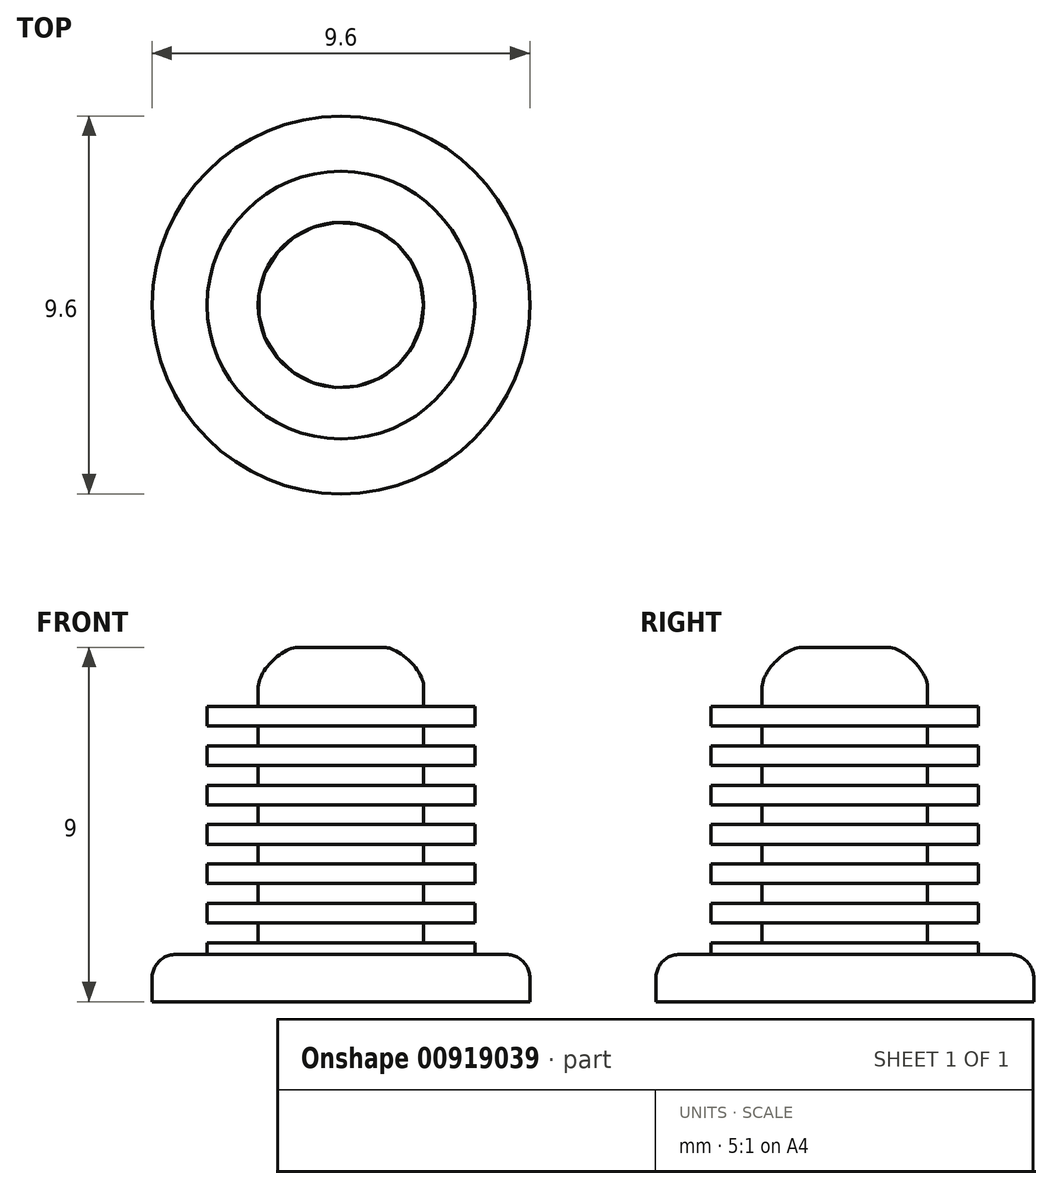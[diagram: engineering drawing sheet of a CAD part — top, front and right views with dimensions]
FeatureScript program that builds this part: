
annotation { "Feature Type Name" : "Feature", "Feature Type Description" : "" }
export const myFeature = defineFeature(function(context is Context, id is Id, definition is map)
    precondition{}
    {
        {
            var Q0;
            Q0=qCreatedBy(makeId("Top.planeOp"),FACE);
            var sketch = newSketch(context, id + "F0", { "sketchPlane" : qUnion([Q0])});
            skCircle(sketch, "E0", {"center": v(0, 0) * mm, "radius": 4.8 * mm});
            skCircle(sketch, "E1", {"center": v(0, 0) * mm, "radius": 2.1 * mm});
            skCircle(sketch, "E2", {"center": v(0, 0) * mm, "radius": 3.4 * mm});
            skSolve(sketch);
        }
        {
            var Q0;
            Q0=makeQuery(id+"F0.imprint","IMPRINT",FACE,{"disambiguationData":[TD([[makeQuery(id+"F0.imprint","IMPRINT",EDGE,{"derivedFrom":sQuery(id+"F0.wireOp",EDGE,"E0")}),1.0]])]});
            var Q1;
            Q1=makeQuery(id+"F0.imprint","IMPRINT",FACE,{"disambiguationData":[TD([[makeQuery(id+"F0.imprint","IMPRINT",EDGE,{"derivedFrom":sQuery(id+"F0.wireOp",EDGE,"E1")}),-1.0]])]});
            extrude(context, id + "F1", {"entities" : qUnion([Q0, Q1]), "depth" : 1.2 * mm, "offsetDistance" : 25 * mm});
        }
        {
            var Q0;
            Q0=makeQuery(id+"F0.imprint","IMPRINT",FACE,{"disambiguationData":[TD([[makeQuery(id+"F0.imprint","IMPRINT",EDGE,{"derivedFrom":sQuery(id+"F0.wireOp",EDGE,"E1")}),1.0]])]});
            var Q1;
            Q1=makeQuery(id+"F0.imprint","IMPRINT",FACE,{"disambiguationData":[TD([[makeQuery(id+"F0.imprint","IMPRINT",EDGE,{"derivedFrom":sQuery(id+"F0.wireOp",EDGE,"E1")}),-1.0]])]});
            extrude(context, id + "F2", {"entities" : qUnion([Q0, Q1]), "operationType" : NewBodyOperationType.ADD, "depth" : 7.5 * mm, "offsetDistance" : 25 * mm});
        }
        {
            var Q0;
            Q0=makeQuery(id+"F0.imprint","IMPRINT",FACE,{"disambiguationData":[TD([[makeQuery(id+"F0.imprint","IMPRINT",EDGE,{"derivedFrom":sQuery(id+"F0.wireOp",EDGE,"E1")}),-1.0]])]});
            extrude(context, id + "F3", {"entities" : qUnion([Q0]), "operationType" : NewBodyOperationType.REMOVE, "depth" : 2 * mm, "offsetDistance" : 25 * mm, "hasSecondDirection" : true, "secondDirectionOppositeDirection" : false, "secondDirectionDepth" : 1.5 * mm});
        }
        {
            var Q0;
            Q0=makeQuery(id+"F0.imprint","IMPRINT",FACE,{"disambiguationData":[TD([[makeQuery(id+"F0.imprint","IMPRINT",EDGE,{"derivedFrom":sQuery(id+"F0.wireOp",EDGE,"E1")}),-1.0]])]});
            extrude(context, id + "F4", {"entities" : qUnion([Q0]), "operationType" : NewBodyOperationType.REMOVE, "depth" : 3 * mm, "offsetDistance" : 25 * mm, "hasSecondDirection" : true, "secondDirectionOppositeDirection" : false, "secondDirectionDepth" : 2.5 * mm});
        }
        {
            var Q0;
            Q0=makeQuery(id+"F0.imprint","IMPRINT",FACE,{"disambiguationData":[TD([[makeQuery(id+"F0.imprint","IMPRINT",EDGE,{"derivedFrom":sQuery(id+"F0.wireOp",EDGE,"E1")}),-1.0]])]});
            var Q1;
            Q1=sQuery(id+"F0.wireOp",EDGE,"E2");
            var Q2;
            Q2=sQuery(id+"F0.wireOp",EDGE,"E1");
            extrude(context, id + "F5", {"entities" : qUnion([Q0]), "operationType" : NewBodyOperationType.REMOVE, "surfaceEntities" : qUnion([Q1, Q2]), "depth" : 4 * mm, "offsetDistance" : 25 * mm, "hasSecondDirection" : true, "secondDirectionOppositeDirection" : false, "secondDirectionDepth" : 3.5 * mm});
        }
        {
            var Q0;
            Q0=makeQuery(id+"F0.imprint","IMPRINT",FACE,{"disambiguationData":[TD([[makeQuery(id+"F0.imprint","IMPRINT",EDGE,{"derivedFrom":sQuery(id+"F0.wireOp",EDGE,"E1")}),-1.0]])]});
            extrude(context, id + "F6", {"entities" : qUnion([Q0]), "operationType" : NewBodyOperationType.REMOVE, "depth" : 5 * mm, "offsetDistance" : 25 * mm, "hasSecondDirection" : true, "secondDirectionOppositeDirection" : false, "secondDirectionDepth" : 4.5 * mm});
        }
        {
            var Q0;
            Q0=makeQuery(id+"F0.imprint","IMPRINT",FACE,{"disambiguationData":[TD([[makeQuery(id+"F0.imprint","IMPRINT",EDGE,{"derivedFrom":sQuery(id+"F0.wireOp",EDGE,"E1")}),-1.0]])]});
            extrude(context, id + "F7", {"entities" : qUnion([Q0]), "operationType" : NewBodyOperationType.REMOVE, "depth" : 6 * mm, "offsetDistance" : 25 * mm, "hasSecondDirection" : true, "secondDirectionOppositeDirection" : false, "secondDirectionDepth" : 5.5 * mm});
        }
        {
            var Q0;
            Q0=makeQuery(id+"F0.imprint","IMPRINT",FACE,{"disambiguationData":[TD([[makeQuery(id+"F0.imprint","IMPRINT",EDGE,{"derivedFrom":sQuery(id+"F0.wireOp",EDGE,"E1")}),1.0]])]});
            extrude(context, id + "F8", {"entities" : qUnion([Q0]), "operationType" : NewBodyOperationType.REMOVE, "depth" : 12 * mm, "offsetDistance" : 25 * mm, "hasSecondDirection" : true, "secondDirectionOppositeDirection" : false, "secondDirectionDepth" : 10 * mm});
        }
        {
            var Q0;
            Q0=makeQuery(id+"F0.imprint","IMPRINT",FACE,{"disambiguationData":[TD([[makeQuery(id+"F0.imprint","IMPRINT",EDGE,{"derivedFrom":sQuery(id+"F0.wireOp",EDGE,"E1")}),-1.0]])]});
            extrude(context, id + "F9", {"entities" : qUnion([Q0]), "operationType" : NewBodyOperationType.REMOVE, "depth" : 7 * mm, "offsetDistance" : 25 * mm, "hasSecondDirection" : true, "secondDirectionOppositeDirection" : false, "secondDirectionDepth" : 6.5 * mm});
        }
        {
            var Q0;
            Q0=makeQuery(id+"F0.imprint","IMPRINT",FACE,{"disambiguationData":[TD([[makeQuery(id+"F0.imprint","IMPRINT",EDGE,{"derivedFrom":sQuery(id+"F0.wireOp",EDGE,"E1")}),1.0]])]});
            extrude(context, id + "F10", {"entities" : qUnion([Q0]), "operationType" : NewBodyOperationType.ADD, "depth" : 9 * mm, "offsetDistance" : 25 * mm});
        }
        {
            var Q0;
            Q0=makeQuery(id+"F10.opExtrude","CAP_EDGE",EDGE,{"disambiguationData":[OSD([sQuery(id+"F0.wireOp",EDGE,"E1")])],"isStart":false});
            fillet(context, id + "F11", {"entities" : qUnion([Q0]), "radius" : 1 * mm, "tangentPropagation" : true, "rho" : .3, "crossSection" : FilletCrossSection.CONIC, "allowEdgeOverflow" : false});
        }
        {
            var Q0;
            Q0=makeQuery(id+"F1.opExtrude","CAP_EDGE",EDGE,{"disambiguationData":[OSD([sQuery(id+"F0.wireOp",EDGE,"E0")])],"isStart":false});
            fillet(context, id + "F12", {"entities" : qUnion([Q0]), "radius" : .6 * mm, "tangentPropagation" : true, "allowEdgeOverflow" : false});
        }
    });
